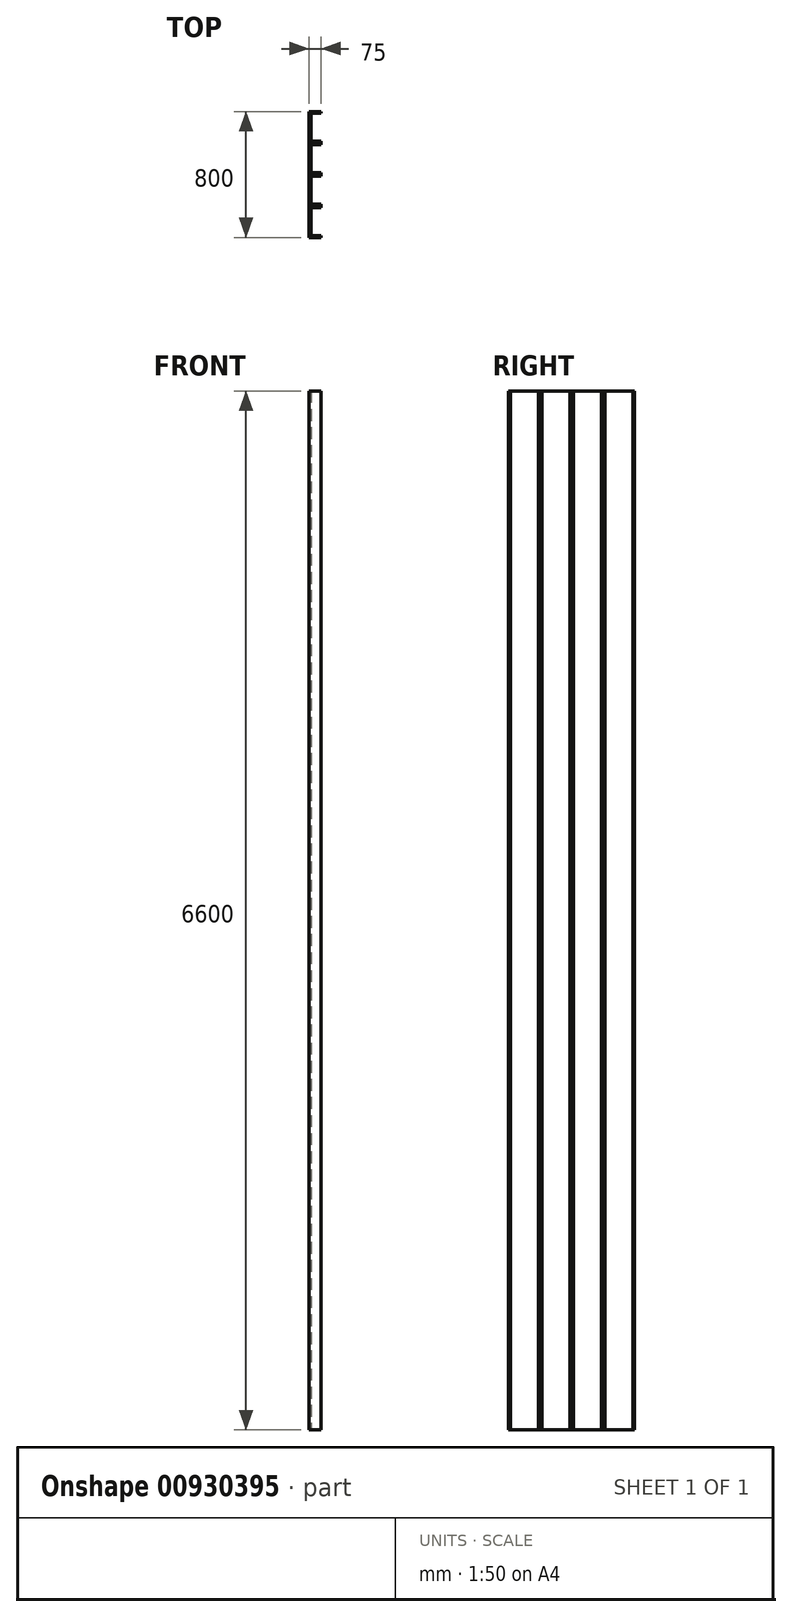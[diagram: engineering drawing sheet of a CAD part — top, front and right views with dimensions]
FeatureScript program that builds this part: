
annotation { "Feature Type Name" : "Feature", "Feature Type Description" : "" }
export const myFeature = defineFeature(function(context is Context, id is Id, definition is map)
    precondition{}
    {
        {
            var Q0;
            Q0=qCreatedBy(makeId("Top.planeOp"),FACE);
            var sketch = newSketch(context, id + "F0", { "sketchPlane" : qUnion([Q0])});
            skLineSegment(sketch, "E0", {"start": v(0, 0) * mm, "end": v(0, 200) * mm});
            skLineSegment(sketch, "E1", {"start": v(0, 200) * mm, "end": v(0, 400) * mm});
            skLineSegment(sketch, "E2", {"start": v(0, 400) * mm, "end": v(0, 600) * mm});
            skLineSegment(sketch, "E3", {"start": v(0, 600) * mm, "end": v(0, 800) * mm});
            skLineSegment(sketch, "E4", {"start": v(0, 800) * mm, "end": v(75, 800) * mm});
            skLineSegment(sketch, "E5", {"start": v(0, 600) * mm, "end": v(75, 600) * mm});
            skLineSegment(sketch, "E6", {"start": v(0, 400) * mm, "end": v(75, 400) * mm});
            skLineSegment(sketch, "E7", {"start": v(0, 200) * mm, "end": v(75, 200) * mm});
            skLineSegment(sketch, "E8", {"start": v(75, 200) * mm, "end": v(75, 188) * mm});
            skLineSegment(sketch, "E9", {"start": v(75, 188) * mm, "end": v(12, 188) * mm});
            skLineSegment(sketch, "E10", {"start": v(12, 188) * mm, "end": v(12, 12) * mm});
            skLineSegment(sketch, "E11", {"start": v(12, 12) * mm, "end": v(75, 12) * mm});
            skLineSegment(sketch, "E12", {"start": v(75, 12) * mm, "end": v(75, 0) * mm});
            skLineSegment(sketch, "E13", {"start": v(75, 0) * mm, "end": v(0, 0) * mm});
            skLineSegment(sketch, "E14", {"start": v(75, 400) * mm, "end": v(75, 388) * mm});
            skLineSegment(sketch, "E15", {"start": v(75, 388) * mm, "end": v(12, 388) * mm});
            skLineSegment(sketch, "E16", {"start": v(12, 388) * mm, "end": v(12, 212) * mm});
            skLineSegment(sketch, "E17", {"start": v(12, 212) * mm, "end": v(75, 212) * mm});
            skLineSegment(sketch, "E18", {"start": v(75, 212) * mm, "end": v(75, 200) * mm});
            skLineSegment(sketch, "E19", {"start": v(75, 600) * mm, "end": v(75, 588) * mm});
            skLineSegment(sketch, "E20", {"start": v(75, 588) * mm, "end": v(12, 588) * mm});
            skLineSegment(sketch, "E21", {"start": v(12, 588) * mm, "end": v(12, 412) * mm});
            skLineSegment(sketch, "E22", {"start": v(12, 412) * mm, "end": v(75, 412) * mm});
            skLineSegment(sketch, "E23", {"start": v(75, 412) * mm, "end": v(75, 400) * mm});
            skLineSegment(sketch, "E24", {"start": v(75, 800) * mm, "end": v(75, 788) * mm});
            skLineSegment(sketch, "E25", {"start": v(75, 788) * mm, "end": v(12, 788) * mm});
            skLineSegment(sketch, "E26", {"start": v(12, 788) * mm, "end": v(12, 612) * mm});
            skLineSegment(sketch, "E27", {"start": v(12, 612) * mm, "end": v(75, 612) * mm});
            skLineSegment(sketch, "E28", {"start": v(75, 612) * mm, "end": v(75, 600) * mm});
            skSolve(sketch);
        }
        {
            var Q0;
            Q0=makeQuery(id+"F0.imprint","IMPRINT",FACE,{"disambiguationData":[TD([[makeQuery(id+"F0.imprint","IMPRINT",EDGE,{"derivedFrom":sQuery(id+"F0.wireOp",EDGE,"E0")}),-1.0]])]});
            extrude(context, id + "F1", {"entities" : qUnion([Q0]), "depth" : 6600 * mm, "offsetDistance" : 25 * mm});
        }
        {
            var Q0;
            Q0=makeQuery(id+"F0.imprint","IMPRINT",FACE,{"disambiguationData":[TD([[makeQuery(id+"F0.imprint","IMPRINT",EDGE,{"derivedFrom":sQuery(id+"F0.wireOp",EDGE,"E1")}),-1.0]])]});
            extrude(context, id + "F2", {"entities" : qUnion([Q0]), "depth" : 6600 * mm, "offsetDistance" : 25 * mm});
        }
        {
            var Q0;
            Q0=makeQuery(id+"F0.imprint","IMPRINT",FACE,{"disambiguationData":[TD([[makeQuery(id+"F0.imprint","IMPRINT",EDGE,{"derivedFrom":sQuery(id+"F0.wireOp",EDGE,"E2")}),-1.0]])]});
            extrude(context, id + "F3", {"entities" : qUnion([Q0]), "depth" : 6600 * mm, "offsetDistance" : 25 * mm});
        }
        {
            var Q0;
            Q0=makeQuery(id+"F0.imprint","IMPRINT",FACE,{"disambiguationData":[TD([[makeQuery(id+"F0.imprint","IMPRINT",EDGE,{"derivedFrom":sQuery(id+"F0.wireOp",EDGE,"E3")}),-1.0]])]});
            extrude(context, id + "F4", {"entities" : qUnion([Q0]), "depth" : 6600 * mm, "offsetDistance" : 25 * mm});
        }
    });
